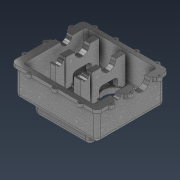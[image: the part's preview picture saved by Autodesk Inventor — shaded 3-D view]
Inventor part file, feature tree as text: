
AUTODESK INVENTOR PART (.ipt)
format: ipt  version: 2022 (Build 260153000, 153)  size: 861,184 bytes
history: native  units: mm
features: extrude x18, sketch x18, fillet x11, projected_geometry x5, hole x3, plane x3, chamfer x2
ambient origin geometry x8: Origin, YZ Plane, XZ Plane, XY Plane, X Axis, Y Axis, Z Axis, Center Point
bodies: Solid1 (feature_tree)
feature tree (60):
  extrude  "Extrusion1"  Depth=350.0mm
  extrude  "Extrusion2"  Depth=20.0mm TaperAngle=0.0deg
  extrude  "Extrusion3"  Depth=10.0mm TaperAngle=0.0deg
  extrude  "Extrusion5"  Depth=68.0mm
  extrude  "Extrusion6"  Depth=23.0mm
  extrude  "Extrusion7"  Depth=150.0mm TaperAngle=0.0deg
  extrude  "Extrusion8"  Depth=108.77mm
  sketch  "Sketch7"  dims[d33=50.0mm d34=150.0mm d35=0.0mm]
  extrude  "Extrusion9"  TaperAngle=0.0deg  [1 undecoded]
  extrude  "Extrusion10"  Depth=4.0mm TaperAngle=0.0deg
  sketch  "Sketch10"  dims[d38=90.0mm d39=0.0mm d40=0.0mm]
  hole  "Hole5"  [1 undecoded]
  extrude  "Extrusion11"  Depth=15.0mm
  extrude  "Extrusion12"  Depth=2.0mm TaperAngle=0.0deg
  extrude  "Extrusion13"  Depth=25.0mm
  extrude  "Extrusion14"  TaperAngle=0.0deg  [1 undecoded]
  extrude  "Extrusion15"  Depth=30.0mm
  fillet  "Fillet1"  Radius=40.0mm
  fillet  "Fillet2"  Radius=21.76mm
  chamfer  "Chamfer1"  Distance=10.0mm
  fillet  "Fillet3"  Radius=10.0mm
  fillet  "Fillet4"  Radius=75.0mm
  fillet  "Fillet5"  Radius=100.0mm
  fillet  "Fillet6"  Radius=250.0mm
  chamfer  "Chamfer2"  Distance=50.0mm
  plane  "Work Plane1"
  extrude  "Extrusion16"  Depth=5.0mm
  fillet  "Fillet7"  Radius=35.0mm
  fillet  "Fillet8"  Radius=35.0mm
  fillet  "Fillet9"  Radius=50.0mm
  hole  "Hole6"  [1 undecoded]
  plane  "Work Plane2"
  extrude  "Extrusion17"  Depth=5.0mm TaperAngle=45.0deg
  fillet  "Fillet11"  Radius=10.0mm
  plane  "Work Plane3"
  extrude  "Extrusion19"  Depth=5.0mm
  extrude  "Extrusion20"  Depth=20.0mm
  fillet  "Fillet12"  Radius=5.0mm
  hole  "Hole7"  [1 undecoded]
  sketch  "Sketch2"  dims[d0=290.0mm d1=350.0mm]
  sketch  "Sketch3"  dims[d19=10.0mm d20=20.0mm d21=0.0mm]
  sketch  "Sketch4"  dims[d22=100.0mm d23=0.0mm d24=10.0mm d25=0.0mm]
  sketch  "Sketch5"  dims[d28=23.172mm d29=68.0mm]
  sketch  "Sketch6"  dims[d30=150.0mm d31=0.0mm d32=23.0mm]
  sketch  "Sketch8"  dims[d36=118.76mm d37=108.77mm]
  sketch  "Sketch11"  dims[d41=105.0mm d42=4.0mm d43=20.0mm d44=0.0mm d45=0.0mm]
  sketch  "Sketch12"  dims[d46=121.5mm d47=121.5mm]
  projected_geometry  "Projected Loop1"
  sketch  "Sketch13"  dims[d48=85.5mm d49=15.0mm]
  sketch  "Sketch14"  dims[d50=20.0mm d51=0.0mm d59=2.0mm d60=0.0mm]
  sketch  "Sketch15"  dims[d82=9.376202mm d83=17.0mm d84=4.0mm d85=2.0mm d86=90.0deg d87=17.0mm d88=20.594885mm d89=25.0mm]
  sketch  "Sketch16"  dims[d90=70.0mm d91=0.0mm d92=0.0mm]
  projected_geometry  "Projected Loop2"
  projected_geometry  "Projected Loop3"
  projected_geometry  "Projected Loop4"
  sketch  "Sketch17"  dims[d93=132.118mm d94=30.0mm d95=40.0mm d96=21.76mm]
  sketch  "Sketch18"  dims[d97=228.068mm d98=10.0mm d99=0.0mm d100=10.0mm d101=0.0mm d105=75.0mm d106=100.0mm d107=250.0mm d108=50.0mm d109=-0.872665mm]
  sketch  "Sketch20"  dims[d110=5.0mm d111=5.0mm d112=35.0mm d113=35.0mm d114=50.0mm d115=-0.872665mm]
  projected_geometry  "Projected Loop5"
  sketch  "Sketch21"  dims[d116=15.0mm d117=20.0mm d118=5.0mm d119=2.0mm d120=45.0deg d121=10.0mm d122=5.0mm d123=20.0mm d124=5.0mm d125=2.0mm d126=45.0deg d127=50.0mm d128=6.0mm d129=10.0mm d130=10.0mm d131=10.0mm d132=10.0mm d134=10.0mm d135=10.0mm d136=10.0mm d137=10.0mm d138=10.0mm d140=20.0mm d143=30.0mm d144=30.0mm d145=90.0mm d146=50.0mm d147=90.0mm d148=90.0mm d149=90.0mm d150=28.75mm d151=28.75mm d153=110.0mm d154=110.0mm d155=15.0mm d156=0.0mm d157=20.0mm d158=5.0mm d159=5.0mm d160=10.0mm d161=6.647mm d162=10.0mm d163=4.0mm d164=2.0mm d165=90.0deg d166=10.0mm d167=20.594885mm d168=70.0mm d169=44.5mm d170=65.0mm d171=145.0mm d172=80.0mm d173=50.0mm d174=24.0mm d175=0.0mm d179=15.0mm d180=116.1mm d181=21.0mm d182=0.0mm d183=21.0mm d184=0.0mm d185=16.0mm d186=9.376202mm d187=17.0mm d188=4.0mm d189=2.0mm d190=90.0deg d191=17.0mm d192=20.594885mm d68=1.0mm d69=1.0mm d70=1.0mm d71=0.15mm d72=0.25mm d73=0.375mm d74=14.3117mm d75=24.0mm d76=20.594885mm d77=0.0625mm d78=0.75mm d79=0.375mm d193=0.0mm d194=0.0mm d195=0.0mm d196=0.0mm]
note: 5 required parameter values undecoded (feature->parameter linkage not recoverable at this tier; creation-order binding heuristic only, values carry confidence <= 0.55)
